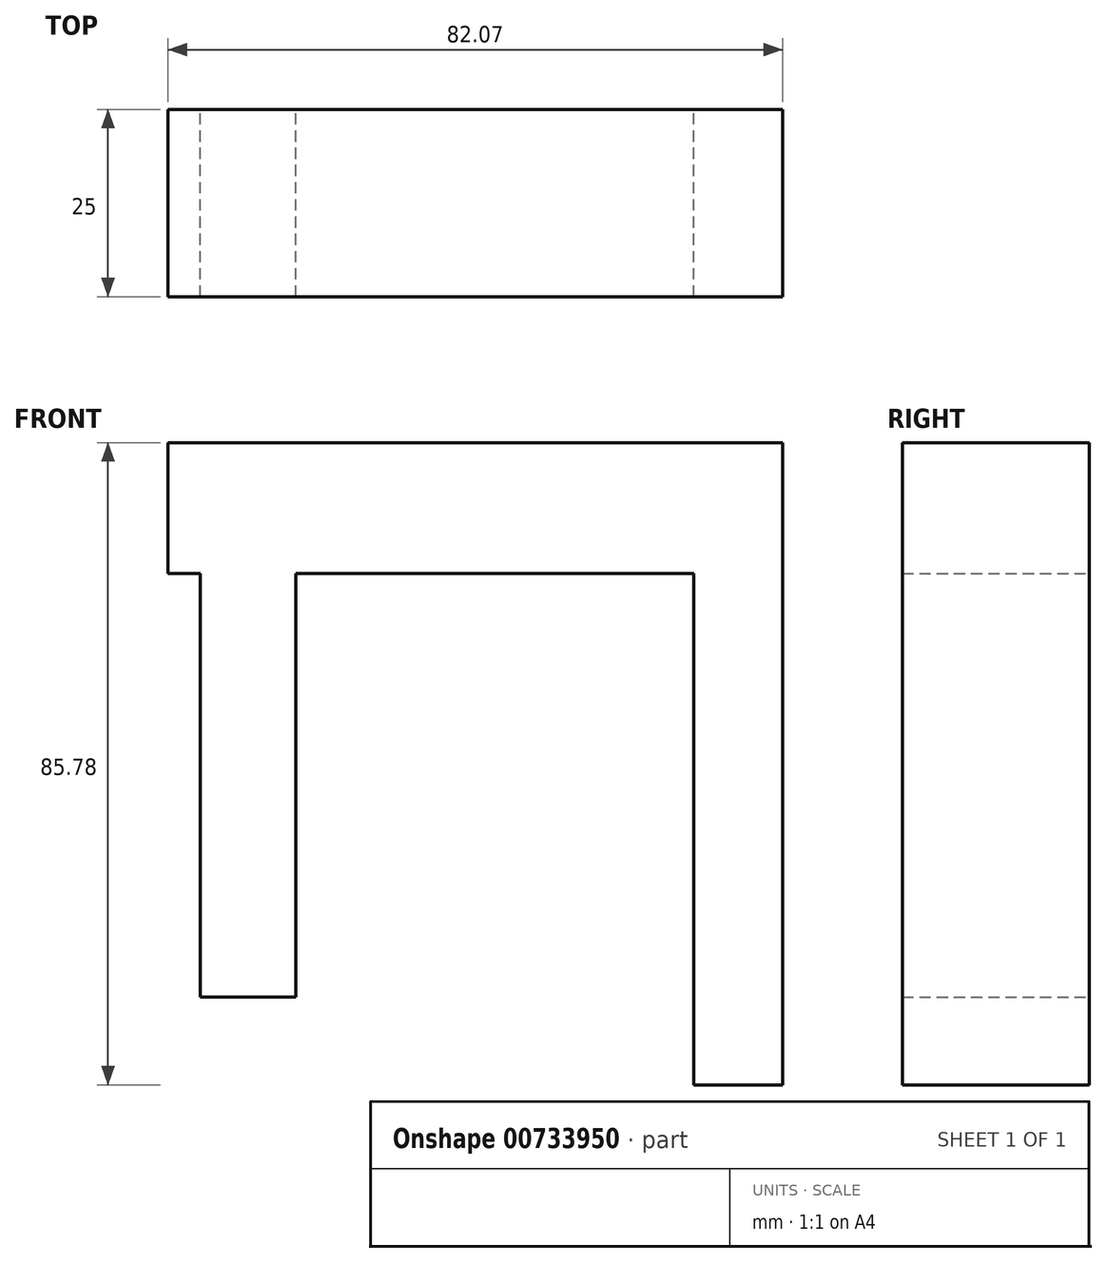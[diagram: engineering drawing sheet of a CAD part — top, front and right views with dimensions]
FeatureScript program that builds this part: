
annotation { "Feature Type Name" : "Feature", "Feature Type Description" : "" }
export const myFeature = defineFeature(function(context is Context, id is Id, definition is map)
    precondition{}
    {
        {
            var Q0;
            Q0=qCreatedBy(makeId("Front.planeOp"),FACE);
            var sketch = newSketch(context, id + "F0", { "sketchPlane" : qUnion([Q0])});
            skLineSegment(sketch, "E0.bottom", {"start": v(-38.25, 51.32) * mm, "end": v(43.82, 51.32) * mm});
            skLineSegment(sketch, "E0.top", {"start": v(-38.25, 33.85) * mm, "end": v(43.82, 33.85) * mm});
            skLineSegment(sketch, "E0.left", {"start": v(-38.25, 51.32) * mm, "end": v(-38.25, 33.85) * mm});
            skLineSegment(sketch, "E0.right", {"start": v(43.82, 51.32) * mm, "end": v(43.82, 33.85) * mm});
            skLineSegment(sketch, "E1.bottom", {"start": v(43.82, 51.32) * mm, "end": v(31.98, 51.32) * mm});
            skLineSegment(sketch, "E1.top", {"start": v(43.82, -34.46) * mm, "end": v(31.98, -34.46) * mm});
            skLineSegment(sketch, "E1.left", {"start": v(43.82, 51.32) * mm, "end": v(43.82, -34.46) * mm});
            skLineSegment(sketch, "E1.right", {"start": v(31.98, 51.32) * mm, "end": v(31.98, -34.46) * mm});
            skSolve(sketch);
        }
        {
            var Q0;
            {var subQ0=sQuery(id+"F0.wireOp",EDGE,"E0.bottom");Q0=makeQuery(id+"F0.imprint","IMPRINT",FACE,{"disambiguationData":[TD([[makeQuery(id+"F0.imprint","IMPRINT",EDGE,{"derivedFrom":subQ0}),-1.0]])]});}
            var Q1;
            {var subQ5=sQuery(id+"F0.wireOp",EDGE,"E1.bottom");Q1=makeQuery(id+"F0.imprint","IMPRINT",FACE,{"disambiguationData":[TD([[makeQuery(id+"F0.imprint","IMPRINT",EDGE,{"derivedFrom":subQ5}),1.0]])]});}
            extrude(context, id + "F1", {"entities" : qUnion([Q0, Q1]), "depth" : 25 * mm, "offsetDistance" : 25 * mm});
        }
        {
            var Q0;
            {var subQ5=sQuery(id+"F0.wireOp",EDGE,"E1.top");Q0=makeQuery(id+"F0.imprint","IMPRINT",FACE,{"disambiguationData":[TD([[makeQuery(id+"F0.imprint","IMPRINT",EDGE,{"derivedFrom":subQ5}),-1.0]])]});}
            var Q1;
            {var subQ5=sQuery(id+"F0.wireOp",EDGE,"E1.bottom");Q1=makeQuery(id+"F0.imprint","IMPRINT",FACE,{"disambiguationData":[TD([[makeQuery(id+"F0.imprint","IMPRINT",EDGE,{"derivedFrom":subQ5}),1.0]])]});}
            extrude(context, id + "F2", {"entities" : qUnion([Q0, Q1]), "operationType" : NewBodyOperationType.ADD, "depth" : 25 * mm, "offsetDistance" : 25 * mm});
        }
        {
            var Q0;
            Q0=qCreatedBy(makeId("Front.planeOp"),FACE);
            var sketch = newSketch(context, id + "F3", { "sketchPlane" : qUnion([Q0])});
            skLineSegment(sketch, "E2.bottom", {"start": v(-33.94, 51.25) * mm, "end": v(-21.15, 51.25) * mm});
            skLineSegment(sketch, "E2.top", {"start": v(-33.94, -22.73) * mm, "end": v(-21.15, -22.73) * mm});
            skLineSegment(sketch, "E2.left", {"start": v(-33.94, 51.25) * mm, "end": v(-33.94, -22.73) * mm});
            skLineSegment(sketch, "E2.right", {"start": v(-21.15, 51.25) * mm, "end": v(-21.15, -22.73) * mm});
            skSolve(sketch);
        }
        {
            var Q0;
            Q0=makeQuery(id+"F3.imprint","IMPRINT",FACE,{"disambiguationData":[TD([[makeQuery(id+"F3.imprint","IMPRINT",EDGE,{"derivedFrom":sQuery(id+"F3.wireOp",EDGE,"E2.bottom")}),-1.0]])]});
            extrude(context, id + "F4", {"entities" : qUnion([Q0]), "operationType" : NewBodyOperationType.ADD, "depth" : 25 * mm, "offsetDistance" : 25 * mm});
        }
    });
